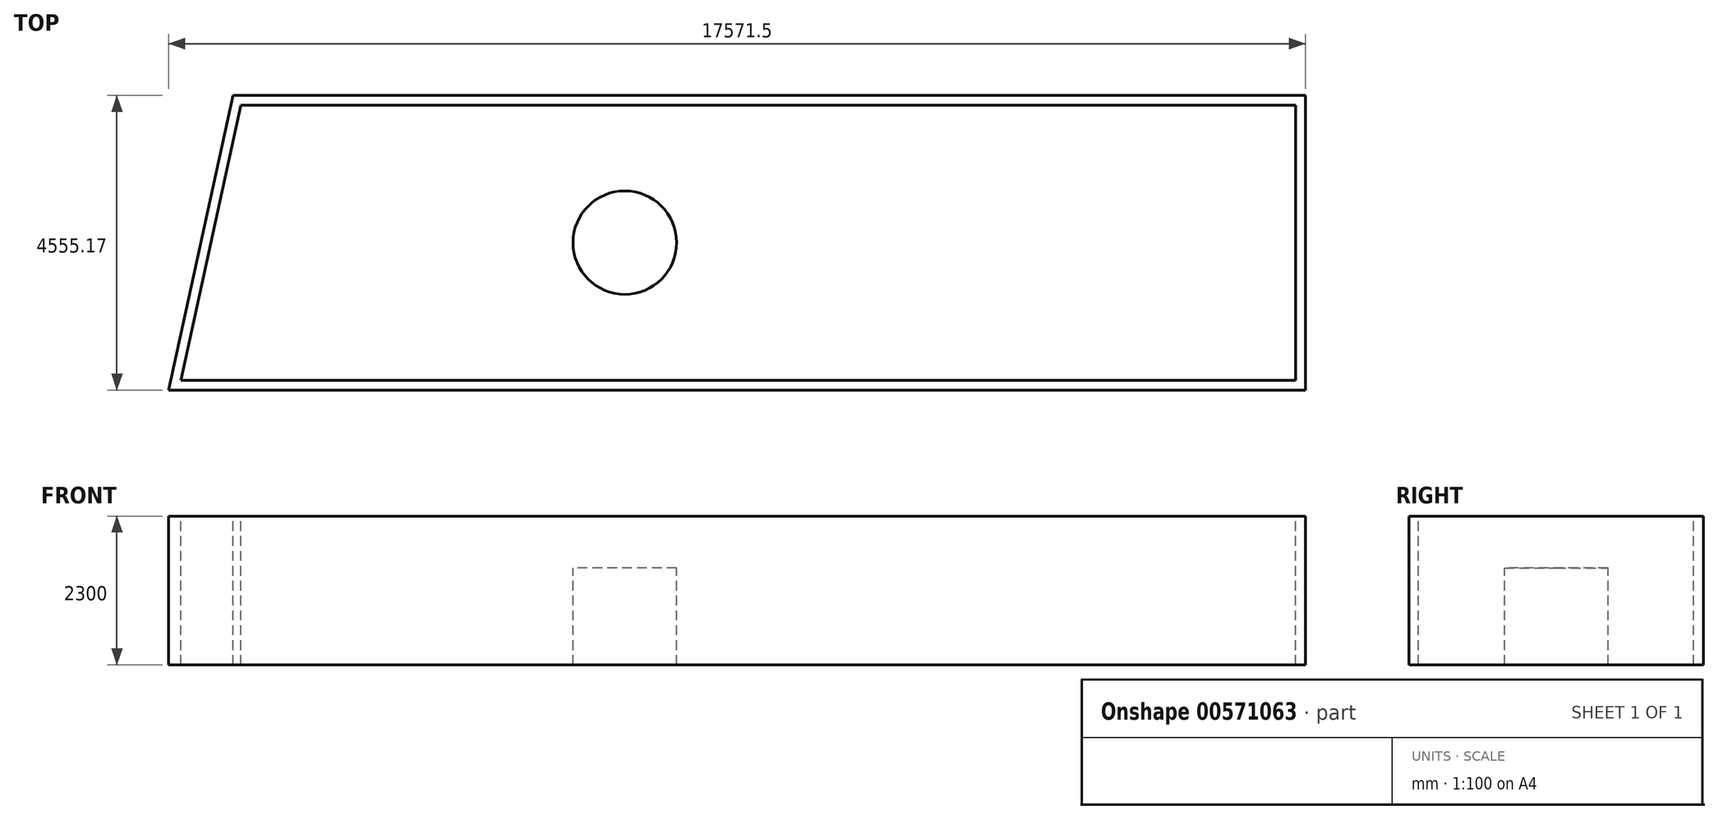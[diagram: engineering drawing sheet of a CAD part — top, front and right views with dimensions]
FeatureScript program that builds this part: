
annotation { "Feature Type Name" : "Feature", "Feature Type Description" : "" }
export const myFeature = defineFeature(function(context is Context, id is Id, definition is map)
    precondition{}
    {
        {
            var Q0;
            Q0=qCreatedBy(makeId("Top.planeOp"),FACE);
            var sketch = newSketch(context, id + "F0", { "sketchPlane" : qUnion([Q0])});
            skLineSegment(sketch, "E0.bottom", {"start": v(7738.49, -5745.18) * mm, "end": v(-9496.73, -5745.18) * mm});
            skLineSegment(sketch, "E0.top", {"start": v(7738.49, -1490) * mm, "end": v(-8568.95, -1490) * mm});
            skLineSegment(sketch, "E0.left", {"start": v(7738.49, -5745.18) * mm, "end": v(7738.49, -1490) * mm});
            skLineSegment(sketch, "E1", {"start": v(-9496.73, -5745.18) * mm, "end": v(-8568.95, -1490) * mm});
            skLineSegment(sketch, "E2.0", {"start": v(-9643.29, -5713.23) * mm, "end": v(-8715.5, -1458.05) * mm});
            skLineSegment(sketch, "E3.0", {"start": v(-9682.96, -5895.18) * mm, "end": v(-8689.77, -1340) * mm});
            skLineSegment(sketch, "E3.1", {"start": v(7888.49, -5895.18) * mm, "end": v(-9682.96, -5895.18) * mm});
            skLineSegment(sketch, "E3.2", {"start": v(7888.49, -5895.18) * mm, "end": v(7888.49, -1340) * mm});
            skLineSegment(sketch, "E3.3", {"start": v(7888.49, -1340) * mm, "end": v(-8689.77, -1340) * mm});
            skSolve(sketch);
        }
        {
            var Q0;
            Q0=sQuery(id+"F0.wireOp",EDGE,"E0.left");
            var Q1;
            Q1=sQuery(id+"F0.wireOp",EDGE,"E3.0");
            var Q2;
            Q2=sQuery(id+"F0.wireOp",EDGE,"E0.bottom");
            var Q3;
            Q3=sQuery(id+"F0.wireOp",EDGE,"E3.3");
            var Q4;
            Q4=sQuery(id+"F0.wireOp",EDGE,"E3.2");
            var Q5;
            Q5=sQuery(id+"F0.wireOp",EDGE,"E1");
            var Q6;
            Q6=sQuery(id+"F0.wireOp",EDGE,"E0.top");
            var Q7;
            Q7=sQuery(id+"F0.wireOp",EDGE,"E3.1");
            extrude(context, id + "F1", {"bodyType" : ToolBodyType.SURFACE, "surfaceEntities" : qUnion([Q0, Q1, Q2, Q3, Q4, Q5, Q6, Q7]), "depth" : 2300 * mm, "offsetDistance" : 25 * mm});
        }
        {
            var Q0;
            Q0=qCreatedBy(makeId("Top.planeOp"),FACE);
            var sketch = newSketch(context, id + "F2", { "sketchPlane" : qUnion([Q0])});
            skCircle(sketch, "E4", {"center": v(-2632.33, -3615.9) * mm, "radius": 800 * mm});
            skSolve(sketch);
        }
        {
            var Q0;
            Q0=sQuery(id+"F2.wireOp",EDGE,"E4");
            extrude(context, id + "F3", {"bodyType" : ToolBodyType.SURFACE, "surfaceEntities" : qUnion([Q0]), "depth" : 1500 * mm, "offsetDistance" : 25 * mm});
        }
    });
